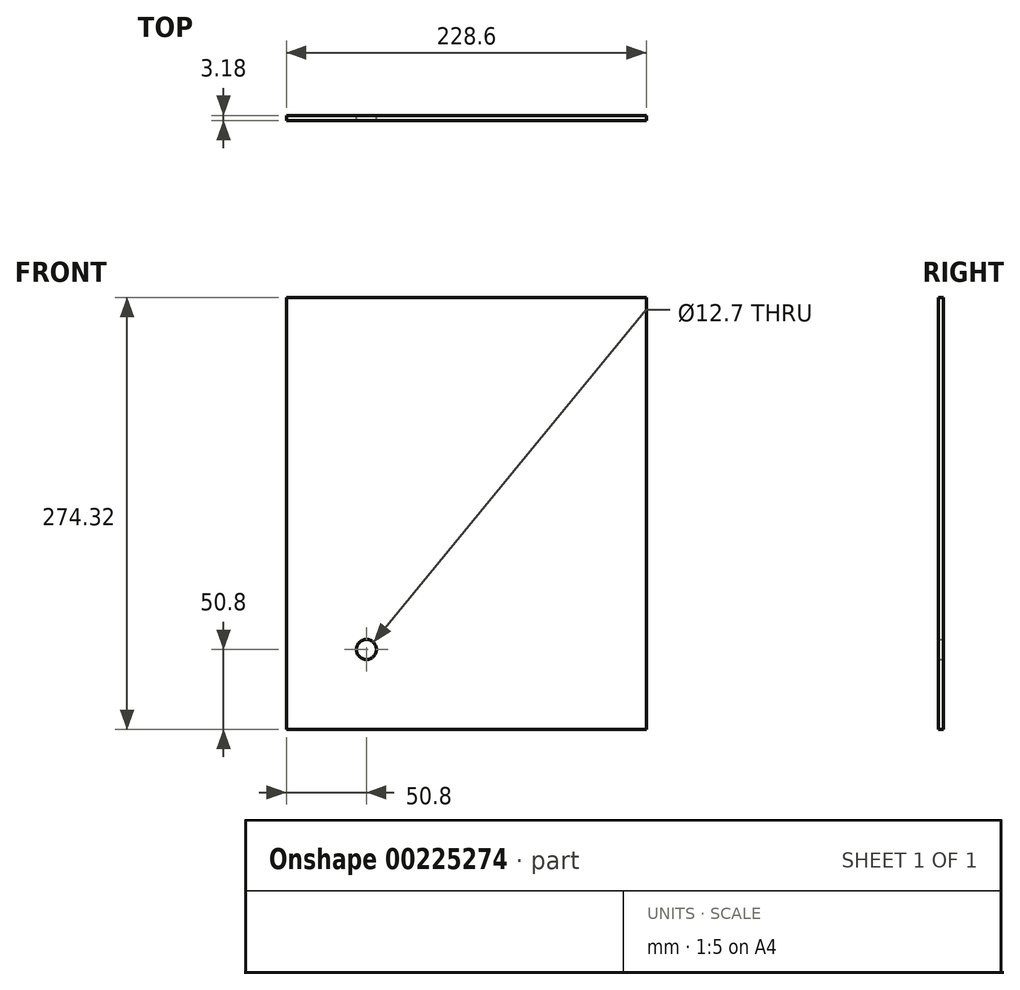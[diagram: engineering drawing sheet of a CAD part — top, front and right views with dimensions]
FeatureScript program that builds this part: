
annotation { "Feature Type Name" : "Feature", "Feature Type Description" : "" }
export const myFeature = defineFeature(function(context is Context, id is Id, definition is map)
    precondition{}
    {
        {
            var Q0;
            Q0=qCreatedBy(makeId("Front.planeOp"),FACE);
            var sketch = newSketch(context, id + "F0", { "sketchPlane" : qUnion([Q0])});
            skLineSegment(sketch, "E0.bottom", {"start": v(0, 0) * mm, "end": v(228.6, 0) * mm});
            skLineSegment(sketch, "E0.top", {"start": v(0, 274.32) * mm, "end": v(228.6, 274.32) * mm});
            skLineSegment(sketch, "E0.left", {"start": v(0, 0) * mm, "end": v(0, 274.32) * mm});
            skLineSegment(sketch, "E0.right", {"start": v(228.6, 0) * mm, "end": v(228.6, 274.32) * mm});
            skCircle(sketch, "E1", {"center": v(50.8, 50.8) * mm, "radius": 6.35 * mm});
            skSolve(sketch);
        }
        {
            var Q0;
            Q0=makeQuery(id+"F0.imprint","IMPRINT",FACE,{"disambiguationData":[TD([[makeQuery(id+"F0.imprint","IMPRINT",EDGE,{"derivedFrom":sQuery(id+"F0.wireOp",EDGE,"E0.bottom")}),1.0]])]});
            extrude(context, id + "F1", {"entities" : qUnion([Q0]), "depth" : 3.17 * mm});
        }
    });
